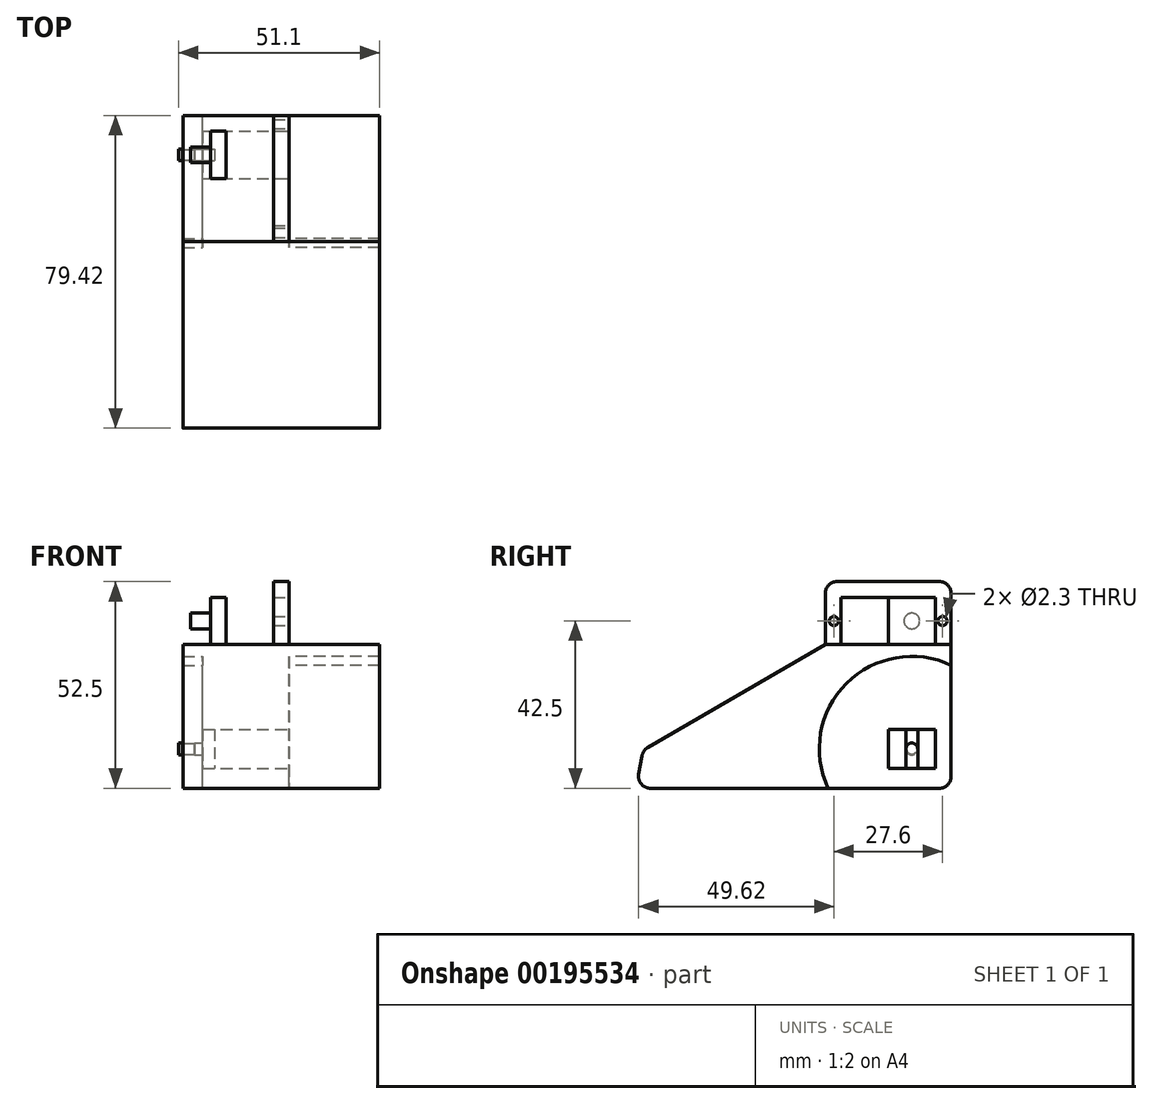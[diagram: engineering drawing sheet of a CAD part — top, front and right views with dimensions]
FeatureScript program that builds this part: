
annotation { "Feature Type Name" : "Feature", "Feature Type Description" : "" }
export const myFeature = defineFeature(function(context is Context, id is Id, definition is map)
    precondition{}
    {
        {
            var Q0;
            Q0=qCreatedBy(makeId("Right.planeOp"),FACE);
            var sketch = newSketch(context, id + "F0", { "sketchPlane" : qUnion([Q0])});
            skLineSegment(sketch, "E0.bottom", {"start": v(-12, 6) * mm, "end": v(12, 6) * mm});
            skLineSegment(sketch, "E0.top", {"start": v(-12, -6) * mm, "end": v(12, -6) * mm});
            skLineSegment(sketch, "E0.left", {"start": v(-12, 6) * mm, "end": v(-12, -6) * mm});
            skLineSegment(sketch, "E0.right", {"start": v(12, 6) * mm, "end": v(12, -6) * mm});
            skPoint(sketch, "E0.middle", {"position": v(0, 0) * mm});
            skLineSegment(sketch, "E1", {"start": v(-16, -6) * mm, "end": v(-16, 7) * mm});
            skLineSegment(sketch, "E2", {"start": v(-13, 10) * mm, "end": v(0, 10) * mm});
            skLineSegment(sketch, "E3", {"start": v(16, -39.5) * mm, "end": v(16, 7) * mm});
            skLineSegment(sketch, "E4", {"start": v(13, 10) * mm, "end": v(0, 10) * mm});
            skLineSegment(sketch, "E5", {"start": v(0, 6) * mm, "end": v(0, 10) * mm, "construction": true});
            skLineSegment(sketch, "E6", {"start": v(-16, 2) * mm, "end": v(-12, 2) * mm, "construction": true});
            skCircle(sketch, "E7", {"center": v(-13.8, 0) * mm, "radius": 1.15 * mm});
            skCircle(sketch, "E8", {"center": v(13.8, 0) * mm, "radius": 1.15 * mm});
            skLineSegment(sketch, "E9", {"start": v(-60.42, -42.5) * mm, "end": v(13, -42.5) * mm});
            skLineSegment(sketch, "E10", {"start": v(0, -6) * mm, "end": v(12, -6) * mm, "construction": true});
            skLineSegment(sketch, "E11.bottom", {"start": v(12, -27.5) * mm, "end": v(0, -27.5) * mm});
            skLineSegment(sketch, "E11.top", {"start": v(12, -37.5) * mm, "end": v(0, -37.5) * mm});
            skLineSegment(sketch, "E11.left", {"start": v(12, -27.5) * mm, "end": v(12, -37.5) * mm});
            skLineSegment(sketch, "E11.right", {"start": v(0, -27.5) * mm, "end": v(0, -37.5) * mm});
            skLineSegment(sketch, "E12", {"start": v(0, -27.5) * mm, "end": v(12, -37.5) * mm, "construction": true});
            skLineSegment(sketch, "E13", {"start": v(6, -37.5) * mm, "end": v(6, -42.5) * mm, "construction": true});
            skLineSegment(sketch, "E14", {"start": v(-16, -6) * mm, "end": v(-12, -6) * mm});
            skLineSegment(sketch, "E15", {"start": v(16, -6) * mm, "end": v(12, -6) * mm});
            skLineSegment(sketch, "E16", {"start": v(-63.38, -38.98) * mm, "end": v(-62.54, -34.24) * mm});
            skPoint(sketch, "E17.endSnap0", {"position": v(6, -40) * mm});
            skLineSegment(sketch, "E18", {"start": v(-64, -42.5) * mm, "end": v(6, -54.3) * mm, "construction": true});
            skCircle(sketch, "E19", {"center": v(6, -32.5) * mm, "radius": 21.5 * mm, "construction": true});
            skPoint(sketch, "E20.visualSharp", {"position": v(-64, -42.5) * mm});
            skArc(sketch, "E20.filletArc", {"start": v(-63.38, -38.98) * mm, "mid": v(-62.72, -41.43) * mm, "end": v(-60.42, -42.5) * mm});
            skPoint(sketch, "E21.visualSharp", {"position": v(-62.26, -32.65) * mm});
            skArc(sketch, "E21.filletArc", {"start": v(-61.1, -32.17) * mm, "mid": v(-62.05, -33.05) * mm, "end": v(-62.54, -34.24) * mm});
            skPoint(sketch, "E22.visualSharp", {"position": v(16, -42.5) * mm});
            skArc(sketch, "E22.filletArc", {"start": v(13, -42.5) * mm, "mid": v(15.12, -41.62) * mm, "end": v(16, -39.5) * mm});
            skPoint(sketch, "E23.visualSharp", {"position": v(-16, 10) * mm});
            skArc(sketch, "E23.filletArc", {"start": v(-13, 10) * mm, "mid": v(-15.12, 9.12) * mm, "end": v(-16, 7) * mm});
            skPoint(sketch, "E24.visualSharp", {"position": v(16, 10) * mm});
            skArc(sketch, "E24.filletArc", {"start": v(16, 7) * mm, "mid": v(15.12, 9.12) * mm, "end": v(13, 10) * mm});
            skLineSegment(sketch, "E25", {"start": v(-61.1, -32.17) * mm, "end": v(-47.9, -24.5) * mm});
            skLineSegment(sketch, "E26", {"start": v(-47.9, -24.5) * mm, "end": v(-25.93, -11.76) * mm});
            skLineSegment(sketch, "E27", {"start": v(-25.93, -11.76) * mm, "end": v(-16, -6) * mm});
            skArc(sketch, "E28", {"start": v(16, -11.23) * mm, "mid": v(-10.62, -15.88) * mm, "end": v(-15.27, -42.5) * mm});
            skLineSegment(sketch, "E29", {"start": v(6, -6) * mm, "end": v(6, -9) * mm, "construction": true});
            skLineSegment(sketch, "E30", {"start": v(12, 2.54) * mm, "end": v(16, 2.54) * mm, "construction": true});
            skLineSegment(sketch, "E31", {"start": v(0, 6) * mm, "end": v(0, -6) * mm, "construction": true});
            skLineSegment(sketch, "E32", {"start": v(-13.8, 0) * mm, "end": v(-12, 0) * mm, "construction": true});
            skLineSegment(sketch, "E33", {"start": v(13.8, 0) * mm, "end": v(12, 0) * mm, "construction": true});
            skLineSegment(sketch, "E34", {"start": v(-13.8, 0) * mm, "end": v(13.8, 0) * mm, "construction": true});
            skSolve(sketch);
        }
        {
            var Q0;
            Q0=makeQuery(id+"F0.imprint","IMPRINT",FACE,{"disambiguationData":[TD([[makeQuery(id+"F0.imprint","IMPRINT",EDGE,{"derivedFrom":sQuery(id+"F0.wireOp",EDGE,"E0.top")}),-1.0]])]});
            extrude(context, id + "F1", {"entities" : qUnion([Q0]), "depth" : 23 * mm});
        }
        {
            var Q0;
            Q0=makeQuery(id+"F0.imprint","IMPRINT",FACE,{"disambiguationData":[TD([[makeQuery(id+"F0.imprint","IMPRINT",EDGE,{"derivedFrom":sQuery(id+"F0.wireOp",EDGE,"E11.bottom")}),-1.0]])]});
            var Q1;
            Q1=makeQuery(id+"F0.imprint","IMPRINT",FACE,{"disambiguationData":[TD([[makeQuery(id+"F0.imprint","IMPRINT",EDGE,{"derivedFrom":sQuery(id+"F0.wireOp",EDGE,"E0.top")}),-1.0]])]});
            extrude(context, id + "F2", {"entities" : qUnion([Q0, Q1]), "operationType" : NewBodyOperationType.ADD, "oppositeDirection" : true, "depth" : 19 * mm});
        }
        {
            var Q0;
            Q0=makeQuery(id+"F2.opExtrude","CAP_FACE",FACE,{"disambiguationData":[OSD([sQuery(id+"F0.wireOp",EDGE,"E0.top"),sQuery(id+"F0.wireOp",EDGE,"E3"),sQuery(id+"F0.wireOp",EDGE,"E9"),sQuery(id+"F0.wireOp",EDGE,"E11.bottom"),sQuery(id+"F0.wireOp",EDGE,"E11.top"),sQuery(id+"F0.wireOp",EDGE,"E11.left"),sQuery(id+"F0.wireOp",EDGE,"E11.right"),sQuery(id+"F0.wireOp",EDGE,"E14"),sQuery(id+"F0.wireOp",EDGE,"E15"),sQuery(id+"F0.wireOp",EDGE,"E16"),sQuery(id+"F0.wireOp",EDGE,"E20.filletArc"),sQuery(id+"F0.wireOp",EDGE,"E21.filletArc"),sQuery(id+"F0.wireOp",EDGE,"E22.filletArc"),sQuery(id+"F0.wireOp",EDGE,"E25"),sQuery(id+"F0.wireOp",EDGE,"E26"),sQuery(id+"F0.wireOp",EDGE,"E27")])],"isStart":false});
            var sketch = newSketch(context, id + "F3", { "sketchPlane" : qUnion([Q0])});
            skLineSegment(sketch, "E35", {"start": v(-12, -27.5) * mm, "end": v(0, -27.5) * mm, "construction": true});
            skLineSegment(sketch, "E36", {"start": v(0, -27.5) * mm, "end": v(-6, -27.5) * mm, "construction": true});
            skLineSegment(sketch, "E37", {"start": v(-6, -27.5) * mm, "end": v(-6, -37.5) * mm, "construction": true});
            skLineSegment(sketch, "E38.bottom", {"start": v(-7.5, -27.5) * mm, "end": v(-4.5, -27.5) * mm});
            skLineSegment(sketch, "E38.top", {"start": v(-7.5, -37.5) * mm, "end": v(-4.5, -37.5) * mm});
            skLineSegment(sketch, "E38.left", {"start": v(-7.5, -27.5) * mm, "end": v(-7.5, -37.5) * mm});
            skLineSegment(sketch, "E38.right", {"start": v(-4.5, -27.5) * mm, "end": v(-4.5, -37.5) * mm});
            skPoint(sketch, "E38.middle", {"position": v(-6, -32.5) * mm});
            skSolve(sketch);
        }
        {
            var Q0;
            Q0=qSketchRegion(id+"F3",true);
            var Q1;
            {var subQ7=sQuery(id+"F3.wireOp",EDGE,"E38.bottom");Q1=makeQuery(id+"F3.imprint","IMPRINT",FACE,{"disambiguationData":[TD([[makeQuery(id+"F3.imprint","IMPRINT",EDGE,{"derivedFrom":subQ7}),1.0]])]});}
            extrude(context, id + "F4", {"entities" : qUnion([Q0, Q1]), "operationType" : NewBodyOperationType.ADD, "depth" : 3 * mm});
        }
        {
            var Q0;
            Q0=makeQuery(id+"F4.opExtrude","CAP_FACE",FACE,{"disambiguationData":[OSD([sQuery(id+"F0.wireOp",EDGE,"E0.top"),sQuery(id+"F0.wireOp",EDGE,"E3"),sQuery(id+"F0.wireOp",EDGE,"E9"),sQuery(id+"F0.wireOp",EDGE,"E11.bottom"),sQuery(id+"F0.wireOp",EDGE,"E11.top"),sQuery(id+"F0.wireOp",EDGE,"E11.left"),sQuery(id+"F0.wireOp",EDGE,"E11.right"),sQuery(id+"F0.wireOp",EDGE,"E14"),sQuery(id+"F0.wireOp",EDGE,"E15"),sQuery(id+"F0.wireOp",EDGE,"E16"),sQuery(id+"F0.wireOp",EDGE,"E20.filletArc"),sQuery(id+"F0.wireOp",EDGE,"E21.filletArc"),sQuery(id+"F0.wireOp",EDGE,"E22.filletArc"),sQuery(id+"F0.wireOp",EDGE,"E25"),sQuery(id+"F0.wireOp",EDGE,"E26"),sQuery(id+"F0.wireOp",EDGE,"E27"),sQuery(id+"F3.wireOp",EDGE,"E38.left"),sQuery(id+"F3.wireOp",EDGE,"E38.right")])],"isStart":false});
            var sketch = newSketch(context, id + "F5", { "sketchPlane" : qUnion([Q0])});
            skLineSegment(sketch, "E39", {"start": v(-7.5, -32.5) * mm, "end": v(-4.5, -32.5) * mm, "construction": true});
            skCircle(sketch, "E40", {"center": v(-6, -32.5) * mm, "radius": 1.5 * mm});
            skSolve(sketch);
        }
        {
            var Q0;
            {var subQ0=sQuery(id+"F5.wireOp",EDGE,"E40");var subQ1=makeQuery(id+"F5.imprint","INTERSECT",VERTEX,{"derivedFrom":[makeQuery(id+"F4.opExtrude","CAP_EDGE",EDGE,{"disambiguationData":[OSD([sQuery(id+"F3.wireOp",EDGE,"E38.left")])],"isStart":false}),subQ0]});Q0=makeQuery(id+"F5.imprint","IMPRINT",FACE,{"disambiguationData":[TD([[makeQuery(id+"F5.imprint","IMPRINT",EDGE,{"disambiguationData":[TD([[subQ1,1.0]])],"derivedFrom":subQ0}),1.0]])]});}
            extrude(context, id + "F6", {"entities" : qUnion([Q0]), "operationType" : NewBodyOperationType.ADD, "depth" : 2 * mm});
        }
        {
            var Q0;
            Q0=makeQuery(id+"F6.opExtrude","CAP_FACE",FACE,{"disambiguationData":[OSD([sQuery(id+"F5.wireOp",EDGE,"E40")])],"isStart":false});
            var sketch = newSketch(context, id + "F7", { "sketchPlane" : qUnion([Q0])});
            skCircle(sketch, "E41", {"center": v(-6, -32.5) * mm, "radius": 1.35 * mm});
            skSolve(sketch);
        }
        {
            var Q0;
            Q0=makeQuery(id+"F7.imprint","IMPRINT",FACE,{"disambiguationData":[TD([[makeQuery(id+"F7.imprint","IMPRINT",EDGE,{"derivedFrom":sQuery(id+"F7.wireOp",EDGE,"E41")}),1.0]])]});
            extrude(context, id + "F8", {"entities" : qUnion([Q0]), "operationType" : NewBodyOperationType.ADD, "depth" : 3.1 * mm});
        }
        {
            var Q0;
            Q0=makeQuery(id+"F8.opExtrude","CAP_FACE",FACE,{"disambiguationData":[OSD([sQuery(id+"F7.wireOp",EDGE,"E41")])],"isStart":false});
            var sketch = newSketch(context, id + "F9", { "sketchPlane" : qUnion([Q0])});
            skCircle(sketch, "E42", {"center": v(-6, -32.5) * mm, "radius": 1.5 * mm});
            skSolve(sketch);
        }
        {
            var Q0;
            Q0=makeQuery(id+"F9.imprint","IMPRINT",FACE,{"disambiguationData":[TD([[makeQuery(id+"F9.imprint","IMPRINT",EDGE,{"derivedFrom":sQuery(id+"F9.wireOp",EDGE,"E42")}),1.0]])]});
            var Q1;
            Q1=makeQuery(id+"F9.imprint","IMPRINT",FACE,{"disambiguationData":[TD([[makeQuery(id+"F9.imprint","IMPRINT",EDGE,{"derivedFrom":makeQuery(id+"F8.opExtrude","CAP_EDGE",EDGE,{"disambiguationData":[OSD([sQuery(id+"F7.wireOp",EDGE,"E41")])],"isStart":false})}),1.0]])]});
            extrude(context, id + "F10", {"entities" : qUnion([Q0, Q1]), "operationType" : NewBodyOperationType.ADD, "depth" : 1 * mm});
        }
        {
            var Q0;
            Q0=makeQuery(id+"F4.opExtrude","CAP_FACE",FACE,{"disambiguationData":[OSD([sQuery(id+"F0.wireOp",EDGE,"E0.top"),sQuery(id+"F0.wireOp",EDGE,"E3"),sQuery(id+"F0.wireOp",EDGE,"E9"),sQuery(id+"F0.wireOp",EDGE,"E11.bottom"),sQuery(id+"F0.wireOp",EDGE,"E11.top"),sQuery(id+"F0.wireOp",EDGE,"E11.left"),sQuery(id+"F0.wireOp",EDGE,"E11.right"),sQuery(id+"F0.wireOp",EDGE,"E14"),sQuery(id+"F0.wireOp",EDGE,"E15"),sQuery(id+"F0.wireOp",EDGE,"E16"),sQuery(id+"F0.wireOp",EDGE,"E20.filletArc"),sQuery(id+"F0.wireOp",EDGE,"E21.filletArc"),sQuery(id+"F0.wireOp",EDGE,"E22.filletArc"),sQuery(id+"F0.wireOp",EDGE,"E25"),sQuery(id+"F0.wireOp",EDGE,"E26"),sQuery(id+"F0.wireOp",EDGE,"E27"),sQuery(id+"F3.wireOp",EDGE,"E38.left"),sQuery(id+"F3.wireOp",EDGE,"E38.right")])],"isStart":false});
            var sketch = newSketch(context, id + "F11", { "sketchPlane" : qUnion([Q0])});
            skCircle(sketch, "E43", {"center": v(-6, -32.5) * mm, "radius": 21.5 * mm, "construction": true});
            skArc(sketch, "E44", {"start": v(15.26, -42.5) * mm, "mid": v(10.61, -15.89) * mm, "end": v(-16, -11.24) * mm});
            skLineSegment(sketch, "E45", {"start": v(-16, -6) * mm, "end": v(-16, -39.5) * mm, "construction": true});
            skLineSegment(sketch, "E46", {"start": v(60.42, -42.5) * mm, "end": v(-13, -42.5) * mm, "construction": true});
            skSolve(sketch);
        }
        {
            var Q0;
            {var subQ2=sQuery(id+"F11.wireOp",EDGE,"E44");Q0=makeQuery(id+"F11.imprint","IMPRINT",FACE,{"disambiguationData":[TD([[makeQuery(id+"F11.imprint","IMPRINT",EDGE,{"derivedFrom":subQ2}),-1.0]])]});}
            extrude(context, id + "F12", {"entities" : qUnion([Q0]), "operationType" : NewBodyOperationType.ADD, "depth" : 5 * mm});
        }
        {
            var Q0;
            {var subQ1=sQuery(id+"F0.wireOp",EDGE,"E0.bottom");Q0=makeQuery(id+"F0.imprint","IMPRINT",FACE,{"disambiguationData":[TD([[makeQuery(id+"F0.imprint","IMPRINT",EDGE,{"derivedFrom":subQ1}),1.0]])]});}
            extrude(context, id + "F13", {"entities" : qUnion([Q0]), "operationType" : NewBodyOperationType.ADD, "oppositeDirection" : true, "depth" : 4 * mm});
        }
        {
            var Q0;
            Q0=qCreatedBy(makeId("Right.planeOp"),FACE);
            cPlane(context, id + "F14", {"entities" : qUnion([Q0]), "cplaneType" : CPlaneType.OFFSET, "offset" : 16 * mm, "oppositeDirection" : true, "width" : 150 * mm, "height" : 150 * mm});
        }
        {
            var Q0;
            Q0=qCreatedBy(id+"F14.planeOp",FACE);
            var sketch = newSketch(context, id + "F15", { "sketchPlane" : qUnion([Q0])});
            skPoint(sketch, "E47.0", {"position": v(12, 0) * mm});
            skLineSegment(sketch, "E48", {"start": v(12, -6) * mm, "end": v(12, 0) * mm});
            skLineSegment(sketch, "E49", {"start": v(12, 0) * mm, "end": v(12, 6) * mm});
            skPoint(sketch, "E50.0", {"position": v(0, 6) * mm});
            skPoint(sketch, "E51.0", {"position": v(0, -6) * mm});
            skLineSegment(sketch, "E52", {"start": v(12, 6) * mm, "end": v(0, 6) * mm});
            skLineSegment(sketch, "E53", {"start": v(0, -6) * mm, "end": v(0, 6) * mm});
            skLineSegment(sketch, "E54", {"start": v(12, 0) * mm, "end": v(0, 0) * mm, "construction": true});
            skLineSegment(sketch, "E55", {"start": v(12, -6) * mm, "end": v(0, -6) * mm});
            skSolve(sketch);
        }
        {
            var Q0;
            Q0=qSketchRegion(id+"F15",true);
            extrude(context, id + "F16", {"entities" : qUnion([Q0]), "operationType" : NewBodyOperationType.ADD, "oppositeDirection" : true, "depth" : 4 * mm});
        }
        {
            var Q0;
            Q0=makeQuery(id+"F16.opExtrude","CAP_FACE",FACE,{"disambiguationData":[OSD([sQuery(id+"F15.wireOp",EDGE,"E48"),sQuery(id+"F15.wireOp",EDGE,"E49"),sQuery(id+"F15.wireOp",EDGE,"E52"),sQuery(id+"F15.wireOp",EDGE,"E53"),sQuery(id+"F15.wireOp",EDGE,"E55")])],"isStart":false});
            var sketch = newSketch(context, id + "F17", { "sketchPlane" : qUnion([Q0])});
            skPoint(sketch, "E56.0", {"position": v(-6, 0) * mm});
            skCircle(sketch, "E57", {"center": v(-6, 0) * mm, "radius": 2 * mm});
            skSolve(sketch);
        }
        {
            var Q0;
            Q0=makeQuery(id+"F17.imprint","IMPRINT",FACE,{"disambiguationData":[TD([[makeQuery(id+"F17.imprint","IMPRINT",EDGE,{"derivedFrom":sQuery(id+"F17.wireOp",EDGE,"E57")}),1.0]])]});
            extrude(context, id + "F18", {"entities" : qUnion([Q0]), "operationType" : NewBodyOperationType.ADD, "depth" : 5 * mm});
        }
    });
